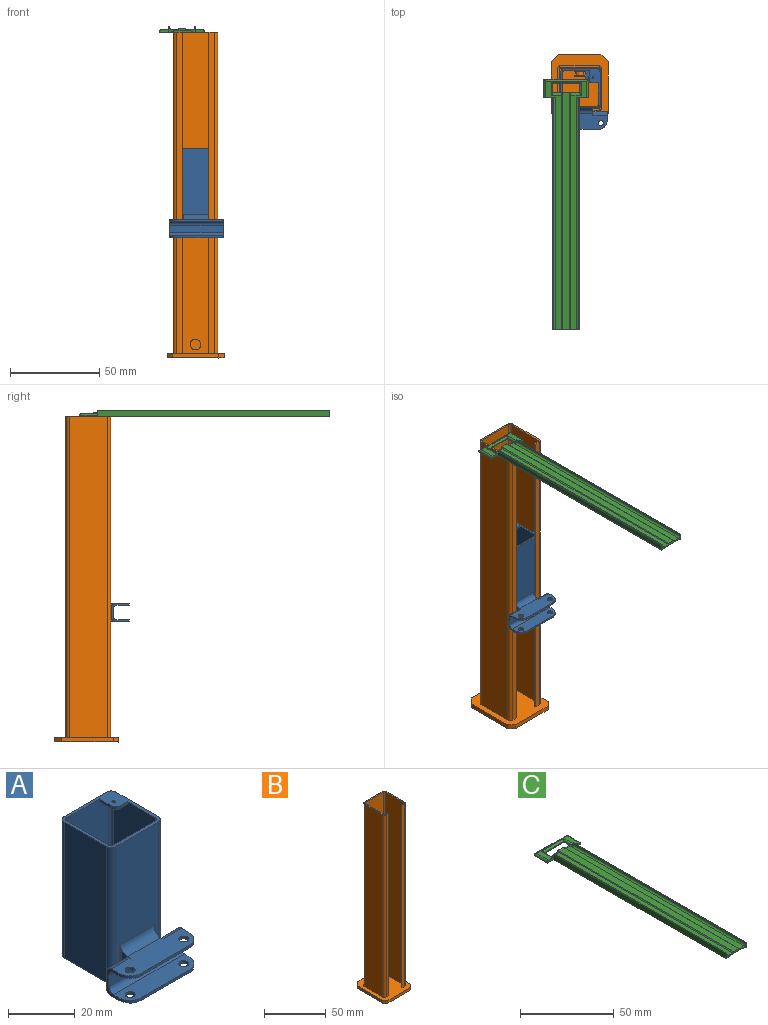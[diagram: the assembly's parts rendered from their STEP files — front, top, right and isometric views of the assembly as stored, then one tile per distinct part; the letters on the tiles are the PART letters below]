
ASSEMBLY  parts=3 mates=2
PART A: 64 faces, bbox 30x34x50 mm
  f0: plane 50x18mm, normal (0,-1,0), area 791.7mm2, adj f2,f4,f13,f18,f21,f48,f49,f50
  f1: plane 50x18mm, normal (-1,0,0), area 888mm2, adj f2,f4,f13,f18,f19,f53,f55,f56
  f2: cylinder r=1mm len=36.23mm, axis (0,0,-1), area 56.9mm2, adj f0,f1,f53,f56
  f3: plane 50x18mm, normal (0,1,0), area 801.7mm2, adj f4,f13,f14,f15,f48,f49,f50,f51
  f4: plane 34x30mm, normal (0,0,-1), area 342.7mm2, adj f0,f1,f3,f8,f9,f10,f11,f12
  f5: plane 30x9mm, normal (0,0,1), area 229.1mm2, adj f22,f23,f26,f29,f30,f32,f33,f38
  f6: plane 30x7mm, normal (0,0,-1), area 185.1mm2, adj f26,f29,f30,f35,f38,f40,f43,f44
  f7: plane 30x7mm, normal (0,0,1), area 185.1mm2, adj f28,f29,f30,f36,f37,f39,f41,f42
  f8: plane 50x18mm, normal (0,-1,0), area 705mm2, adj f4,f13,f16,f17,f45,f46,f47
  f9: plane 50x18mm, normal (0,1,0), area 900mm2, adj f4,f13,f19,f20
  f10: plane 50x18mm, normal (1,0,0), area 900mm2, adj f4,f13,f14,f17
  f11: plane 50x18mm, normal (-1,0,0), area 900mm2, adj f4,f13,f15,f16
  f12: plane 50x18mm, normal (1,0,0), area 900mm2, adj f4,f13,f20,f21
  f13: plane 22x22mm, normal (0,0,1), area 114.6mm2, adj f0,f1,f3,f8,f9,f10,f11,f12
  f14: cylinder r=2mm len=50mm, axis (0,0,1), area 157.1mm2, adj f3,f4,f10,f13
  f15: cylinder r=2mm len=50mm, axis (0,0,-1), area 157.1mm2, adj f3,f4,f11,f13
  f16: cylinder r=2mm len=50mm, axis (0,0,1), area 157.1mm2, adj f4,f8,f11,f13
  f17: cylinder r=2mm len=50mm, axis (0,0,-1), area 157.1mm2, adj f4,f8,f10,f13
  f18: cylinder r=1mm len=11.77mm, axis (0,0,-1), area 18.5mm2, adj f0,f1,f4,f57
  f19: cylinder r=1mm len=50mm, axis (0,0,1), area 78.5mm2, adj f1,f4,f9,f13
  f20: cylinder r=1mm len=50mm, axis (0,0,-1), area 78.5mm2, adj f4,f9,f12,f13
  f21: cylinder r=1mm len=50mm, axis (0,0,1), area 78.5mm2, adj f0,f4,f12,f13
  f22: plane 11.34x3.5mm, normal (-1,0,0), area 17.7mm2, adj f4,f5,f25,f31,f32,f45,f46
  f23: plane 11.34x3.5mm, normal (1,0,0), area 17.7mm2, adj f4,f5,f24,f33,f34,f45,f47
  f24: plane 8x6mm, normal (0,1,0), area 48mm2, adj f23,f29,f33,f34
  f25: plane 8x6mm, normal (0,1,0), area 48mm2, adj f22,f30,f31,f32
  f26: plane 20x1mm, normal (0,-1,0), area 20mm2, adj f5,f6,f38,f40
  f27: plane 30x4mm, normal (0,-1,0), area 120mm2, adj f29,f30,f35,f36
  f28: plane 20x1mm, normal (0,-1,0), area 20mm2, adj f4,f7,f37,f39
  f29: plane 10x5mm, normal (1,0,0), area 18mm2, adj f4,f5,f6,f7,f24,f27,f33,f34
  f30: plane 10x5mm, normal (-1,0,0), area 18mm2, adj f4,f5,f6,f7,f25,f27,f31,f32
  f31: cylinder r=2mm len=8mm, axis (1,0,0), area 25.1mm2, adj f4,f22,f25,f30
  f32: cylinder r=2mm len=8mm, axis (1,0,0), area 25.1mm2, adj f5,f22,f25,f30
  f33: cylinder r=2mm len=8mm, axis (1,0,0), area 25.1mm2, adj f5,f23,f24,f29
  f34: cylinder r=2mm len=8mm, axis (1,0,0), area 25.1mm2, adj f4,f23,f24,f29
  f35: cylinder r=2mm len=30mm, axis (-1,0,0), area 94.2mm2, adj f6,f27,f29,f30
  f36: cylinder r=2mm len=30mm, axis (1,0,0), area 94.2mm2, adj f7,f27,f29,f30
  f37: cylinder r=5mm len=5mm, axis (0,0,-1), area 7.9mm2, adj f4,f7,f28,f30
  f38: cylinder r=5mm len=5mm, axis (0,0,-1), area 7.9mm2, adj f5,f6,f26,f30
  f39: cylinder r=5mm len=5mm, axis (0,0,1), area 7.9mm2, adj f4,f7,f28,f29
  f40: cylinder r=5mm len=5mm, axis (0,0,1), area 7.9mm2, adj f5,f6,f26,f29
  f41: cylinder r=1.5mm len=3mm, axis (0,0,1), area 9.4mm2, adj f4,f7
  f42: cylinder r=1.5mm len=3mm, axis (0,0,1), area 9.4mm2, adj f4,f7
  f43: cylinder r=1.5mm len=3mm, axis (0,0,1), area 9.4mm2, adj f5,f6
  f44: cylinder r=1.5mm len=3mm, axis (0,0,1), area 9.4mm2, adj f5,f6
  f45: cylinder r=3mm len=15mm, axis (-1,0,0), area 66.9mm2, adj f5,f8,f22,f23,f46,f47
  f46: cylinder r=0.5mm len=13mm, axis (0,0,-1), area 9.6mm2, adj f4,f8,f22,f45
  f47: cylinder r=0.5mm len=13mm, axis (0,0,1), area 9.6mm2, adj f4,f8,f23,f45
  f48: plane 8x1mm, normal (1,0,0), area 8mm2, adj f0,f3,f4,f51
  f49: plane 6x1mm, normal (0,0,-1), area 6mm2, adj f0,f3,f51,f52
  f50: plane 8x1mm, normal (-1,0,0), area 8mm2, adj f0,f3,f4,f52
  f51: cylinder r=2mm len=2mm, axis (0,1,0), area 3.1mm2, adj f0,f3,f48,f49
  f52: cylinder r=2mm len=2mm, axis (0,-1,0), area 3.1mm2, adj f0,f3,f49,f50
  f53: plane 7x5mm, normal (0,0,-1), area 33.1mm2, adj f0,f1,f2,f54,f55,f60,f63
  f54: plane 5x1mm, normal (-1,0,0), area 5mm2, adj f0,f13,f53,f63
  f55: plane 3x1mm, normal (0,-1,0), area 3mm2, adj f1,f13,f53,f63
  f56: plane 7x7mm, normal (0,0,1), area 47.1mm2, adj f0,f1,f2,f58,f59,f61,f62
  f57: plane 7x7mm, normal (0,0,-1), area 47.1mm2, adj f0,f1,f18,f58,f59,f61,f62
  f58: plane 5x1mm, normal (-1,0,0), area 5mm2, adj f0,f56,f57,f62
  f59: plane 5x1mm, normal (0,-1,0), area 5mm2, adj f1,f56,f57,f62
  f60: cylinder r=0.5mm len=1mm, axis (0,0,1), area 3.1mm2, adj f13,f53
  f61: cylinder r=0.5mm len=1mm, axis (0,0,-1), area 3.1mm2, adj f56,f57
  f62: cylinder r=2mm len=2mm, axis (0,0,1), area 3.1mm2, adj f56,f57,f58,f59
  f63: cylinder r=2mm len=2mm, axis (0,0,1), area 3.1mm2, adj f13,f53,f54,f55
PART B: 37 faces, bbox 32x36x182.5 mm
  f0: cylinder r=3mm len=6mm, axis (0,1,0), area 37.7mm2, adj f7,f29
  f1: plane 36x32mm, normal (0,0,1), area 1048.6mm2, adj f2,f3,f4,f5,f7,f8,f9,f10
  f2: plane 29x2.5mm, normal (1,0,0), area 72.5mm2, adj f1,f6,f33,f36
  f3: plane 24x2.5mm, normal (0,1,0), area 60mm2, adj f1,f6,f35,f36
  f4: plane 29x2.5mm, normal (-1,0,0), area 72.5mm2, adj f1,f6,f34,f35
  f5: plane 26x2.5mm, normal (0,-1,0), area 65mm2, adj f1,f6,f33,f34
  f6: plane 36x32mm, normal (0,0,-1), area 1127mm2, adj f2,f3,f4,f5,f33,f34,f35,f36
  f7: plane 180x21mm, normal (0,-1,0), area 3751.7mm2, adj f0,f1,f19,f20,f23
  f8: plane 180x21mm, normal (-1,0,0), area 3780mm2, adj f1,f19,f20,f21
  f9: plane 180x3mm, normal (0,1,0), area 540mm2, adj f1,f10,f19,f21
  f10: plane 180x1mm, normal (-1,0,0), area 180mm2, adj f1,f9,f11,f19
  f11: plane 180x3mm, normal (0,-1,0), area 540mm2, adj f1,f10,f19,f24
  f12: plane 180x21mm, normal (1,0,0), area 3780mm2, adj f1,f19,f24,f25
  f13: plane 180x21mm, normal (0,1,0), area 3780mm2, adj f1,f19,f25,f26
  f14: plane 180x21mm, normal (-1,0,0), area 3780mm2, adj f1,f19,f26,f27
  f15: plane 180x3mm, normal (0,-1,0), area 540mm2, adj f1,f16,f19,f27
  f16: plane 180x1mm, normal (1,0,0), area 180mm2, adj f1,f15,f17,f19
  f17: plane 180x3mm, normal (0,1,0), area 540mm2, adj f1,f16,f19,f22
  f18: plane 180x21mm, normal (1,0,0), area 3780mm2, adj f1,f19,f22,f23
  f19: plane 25x25mm, normal (0,0,1), area 78.4mm2, adj f7,f8,f9,f10,f11,f12,f13,f14
  f20: cylinder r=1mm len=180mm, axis (0,0,-1), area 282.7mm2, adj f1,f7,f8,f19
  f21: cylinder r=1mm len=180mm, axis (0,0,1), area 282.7mm2, adj f1,f8,f9,f19
  f22: cylinder r=1mm len=180mm, axis (0,0,-1), area 282.7mm2, adj f1,f17,f18,f19
  f23: cylinder r=1mm len=180mm, axis (0,0,1), area 282.7mm2, adj f1,f7,f18,f19
  f24: cylinder r=2mm len=180mm, axis (0,0,-1), area 565.5mm2, adj f1,f11,f12,f19
  f25: cylinder r=2mm len=180mm, axis (0,0,1), area 565.5mm2, adj f1,f12,f13,f19
  f26: cylinder r=2mm len=180mm, axis (0,0,-1), area 565.5mm2, adj f1,f13,f14,f19
  f27: cylinder r=2mm len=180mm, axis (0,0,1), area 565.5mm2, adj f1,f14,f15,f19
  f28: cylinder r=2.25mm len=4.5mm, axis (0,-1,0), area 28.3mm2, adj f29,f30
  f29: plane 6x6mm, normal (0,-1,0), area 12.4mm2, adj f0,f28
  f30: plane 6x6mm, normal (0,1,0), area 12.4mm2, adj f28,f32
  f31: plane 6x6mm, normal (0,-1,0), area 28.3mm2, adj f32
  f32: cylinder r=3mm len=6mm, axis (0,1,0), area 18.8mm2, adj f30,f31
  f33: plane 3x3mm, normal (0.71,-0.71,0), area 10.6mm2, adj f1,f2,f5,f6
  f34: plane 3x3mm, normal (-0.71,-0.71,0), area 10.6mm2, adj f1,f4,f5,f6
  f35: plane 4x4mm, normal (-0.71,0.71,0), area 14.1mm2, adj f1,f3,f4,f6
  f36: plane 4x4mm, normal (0.71,0.71,0), area 14.1mm2, adj f1,f2,f3,f6
PART C: 43 faces, bbox 25.1x140.1x3.6 mm
  f0: plane 139x23mm, normal (0,0,1), area 985.7mm2, adj f1,f2,f15,f16,f17,f18,f19,f20
  f1: plane 5x1.5mm, normal (0,-1,0), area 7.3mm2, adj f0,f3,f4,f20,f31
  f2: plane 5x1.5mm, normal (0,-1,0), area 7.3mm2, adj f0,f3,f6,f22,f27
  f3: plane 140x25mm, normal (0,0,-1), area 305mm2, adj f1,f2,f4,f5,f6,f7,f8,f9
  f4: plane 10x0.5mm, normal (1,0,0), area 5mm2, adj f1,f3,f5,f20
  f5: plane 25x0.5mm, normal (0,1,0), area 12.5mm2, adj f3,f4,f6,f21
  f6: plane 10x0.5mm, normal (-1,0,0), area 5mm2, adj f2,f3,f5,f22
  f7: plane 14x0.75mm, normal (0,-1,0), area 9mm2, adj f3,f28,f29,f30,f35,f36
  f8: plane 15.14x2.14mm, normal (0,1,0), area 9.6mm2, adj f3,f9,f11,f12,f13,f14,f15,f16
  f9: plane 5.06x0.5mm, normal (-1,0,0), area 2.5mm2, adj f3,f8,f10,f16,f17
  f10: plane 15x0.5mm, normal (0,-1,0), area 7.5mm2, adj f3,f9,f11,f19
  f11: plane 5.06x0.5mm, normal (1,0,0), area 2.5mm2, adj f3,f8,f10,f15,f18
  f12: plane 1.4x0.62mm, normal (1,0,0), area 0.3mm2, adj f8,f14,f42
  f13: plane 1.4x0.62mm, normal (-1,0,0), area 0.3mm2, adj f8,f14,f40
  f14: plane 132.5x4mm, normal (0,0,1), area 530mm2, adj f8,f12,f13,f34,f39,f41
  f15: cylinder r=1.4mm len=6mm, axis (-1,0,0), area 11.7mm2, adj f0,f8,f11,f18,f40
  f16: cylinder r=1.4mm len=6mm, axis (-1,0,0), area 11.7mm2, adj f0,f8,f9,f17,f42
  f17: cylinder r=1mm len=7.4mm, axis (0,-1,0), area 9.6mm2, adj f0,f9,f16,f19
  f18: cylinder r=1mm len=7.4mm, axis (0,1,0), area 9.6mm2, adj f0,f11,f15,f19
  f19: cylinder r=1mm len=17mm, axis (1,0,0), area 24.7mm2, adj f0,f10,f17,f18
  f20: cylinder r=1mm len=10mm, axis (0,-1,0), area 15.1mm2, adj f0,f1,f4,f21
  f21: cylinder r=1mm len=25mm, axis (1,0,0), area 38.1mm2, adj f0,f5,f20,f22
  f22: cylinder r=1mm len=10mm, axis (0,1,0), area 15.1mm2, adj f0,f2,f6,f21
  f23: plane 2x1.5mm, normal (0,1,0), area 1.2mm2, adj f0,f31,f32,f33,f38
  f24: plane 2x1.5mm, normal (0,1,0), area 1.2mm2, adj f0,f25,f26,f27,f37
  f25: plane 130x1mm, normal (1,0,0), area 130mm2, adj f24,f26,f34,f37
  f26: plane 130x0.5mm, normal (0,0,1), area 65mm2, adj f24,f25,f27,f34
  f27: plane 130x3.5mm, normal (-1,0,0), area 455mm2, adj f2,f3,f24,f26,f34
  f28: plane 130x0.95mm, normal (0.37,0,-0.93), area 133.5mm2, adj f3,f7,f34,f36
  f29: plane 130x8.35mm, normal (0,0,-1), area 1085mm2, adj f7,f34,f35,f36
  f30: plane 130x0.95mm, normal (-0.37,0,-0.93), area 133.5mm2, adj f3,f7,f34,f35
  f31: plane 130x3.5mm, normal (1,0,0), area 455mm2, adj f1,f3,f23,f32,f34
  f32: plane 130x0.5mm, normal (0,0,1), area 65mm2, adj f23,f31,f33,f34
  f33: plane 130x1mm, normal (-1,0,0), area 130mm2, adj f23,f32,f34,f38
  f34: plane 15x3.5mm, normal (0,-1,0), area 18mm2, adj f0,f3,f14,f25,f26,f27,f28,f29
  f35: cylinder r=5mm len=130mm, axis (0,-1,0), area 249.9mm2, adj f7,f29,f30,f34
  f36: cylinder r=5mm len=130mm, axis (0,1,0), area 249.9mm2, adj f7,f28,f29,f34
  f37: cylinder r=1mm len=130mm, axis (0,-1,0), area 204.2mm2, adj f0,f24,f25,f34
  f38: cylinder r=1mm len=130mm, axis (0,1,0), area 204.2mm2, adj f0,f23,f33,f34
  f39: cylinder r=0.5mm len=131.1mm, axis (0,-1,0), area 103mm2, adj f0,f14,f34,f40
  f40: torus R=1.9mm, axis (1,0,0), area 1.5mm2, adj f8,f13,f15,f39
  f41: cylinder r=0.5mm len=131.1mm, axis (0,1,0), area 103mm2, adj f0,f14,f34,f42
  f42: torus R=1.9mm, axis (1,0,0), area 1.5mm2, adj f8,f12,f16,f41
PLACE A rot(axis=(0.92,0.07,-0.38),0deg) t=(-109.44,87.41,-1.37)mm
PLACE B rot(axis=(0.92,0.07,-0.38),0deg) t=(-109.94,87.41,-66.37)mm
PLACE C rot(axis=(0.92,0.07,-0.38),0deg) t=(-117.44,87.21,114.38)mm
MATE fastened A.f10 <-> B.f8  axis (1,0,0) through (-98.44,87.41,23.63)mm
MATE fastened C.f3 <-> B.f19  axis (0,0,-1) through (-109.94,89.71,113.63)mm
